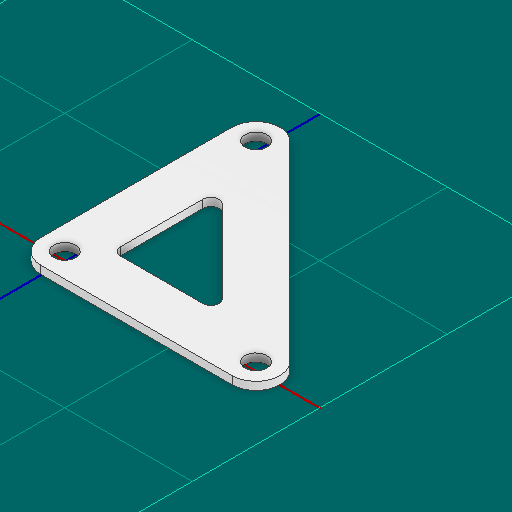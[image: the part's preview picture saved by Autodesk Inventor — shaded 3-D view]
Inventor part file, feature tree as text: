
AUTODESK INVENTOR PART (.ipt)
format: ipt  version: 2025 (Build 290162000, 162)  size: 131,584 bytes
history: native  units: in
note: dims shown in document units (in); Inventor stores cm internally (conversion verified against a paired STEP export)
features: other x6, sketch x1
ambient origin geometry x8: Origin, YZ Plane, XZ Plane, XY Plane, X Axis, Y Axis, Z Axis, Center Point
bodies: Solid1 (feature_tree)
feature tree (7):
  other  "right_angle_gusset.ipt"
  other  "Blocks"
  other  "main"
  other  "Solid1::right_angle_gusset.ipt"
  other  "TaggingFeature1"
  sketch  "Sketch1"  dims[d0=0.3937in d1=0.375in d2=0.375in d5=0.375in d6=0.0625in d7=0.0625in]
  other  "main:1"
